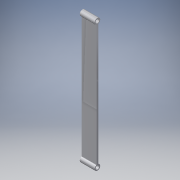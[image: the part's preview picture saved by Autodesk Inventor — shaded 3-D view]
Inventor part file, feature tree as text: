
AUTODESK INVENTOR PART (.ipt)
format: ipt  version: 2016 (Build 200138000, 138)  size: 102,400 bytes
history: native  units: in
note: dims shown in document units (in); Inventor stores cm internally (conversion verified against a paired STEP export)
features: extrude x1, sketch x1
ambient origin geometry x8: Origin, YZ Plane, XZ Plane, XY Plane, X Axis, Y Axis, Z Axis, Center Point
bodies: Solid1 (feature_tree)
feature tree (2):
  extrude  "Extrusion1"  Depth=1.0in
  sketch  "Sketch1"  dims[d0=0.125in d2=0.25in d3=0.25in d4=0.0625in d5=0.0625in d6=1.0in d7=0.0in d8=8.5in]
